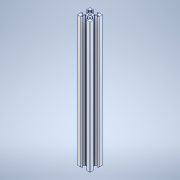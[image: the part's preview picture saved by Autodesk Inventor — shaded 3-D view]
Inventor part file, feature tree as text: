
AUTODESK INVENTOR PART (.ipt)
format: ipt  version: 2021 (Build 250183000, 183)  size: 236,544 bytes
history: native  units: mm
features: sketch x3, extrude x2, fillet x2, other x1, pattern_circular x1, hole x1, projected_geometry x1
ambient origin geometry x8: Origin, YZ Plane, XZ Plane, XY Plane, X Axis, Y Axis, Z Axis, Center Point
bodies: Body1 (feature_tree)
feature tree (11):
  other  "實體1"
  extrude  "擠出1"  Depth=20.0mm
  extrude  "擠出2"  Depth=20.0mm
  fillet  "圓角1"  Radius=210.0mm
  pattern_circular  "環形陣列1"  [2 undecoded]
  hole  "孔1"  [1 undecoded]
  fillet  "圓角2"  Radius=6.2mm
  sketch  "草圖1"
  sketch  "草圖2"
  projected_geometry  "投影迴路1"
  sketch  "草圖3"
note: 3 required parameter values undecoded (feature->parameter linkage not recoverable at this tier; creation-order binding heuristic only, values carry confidence <= 0.55)
